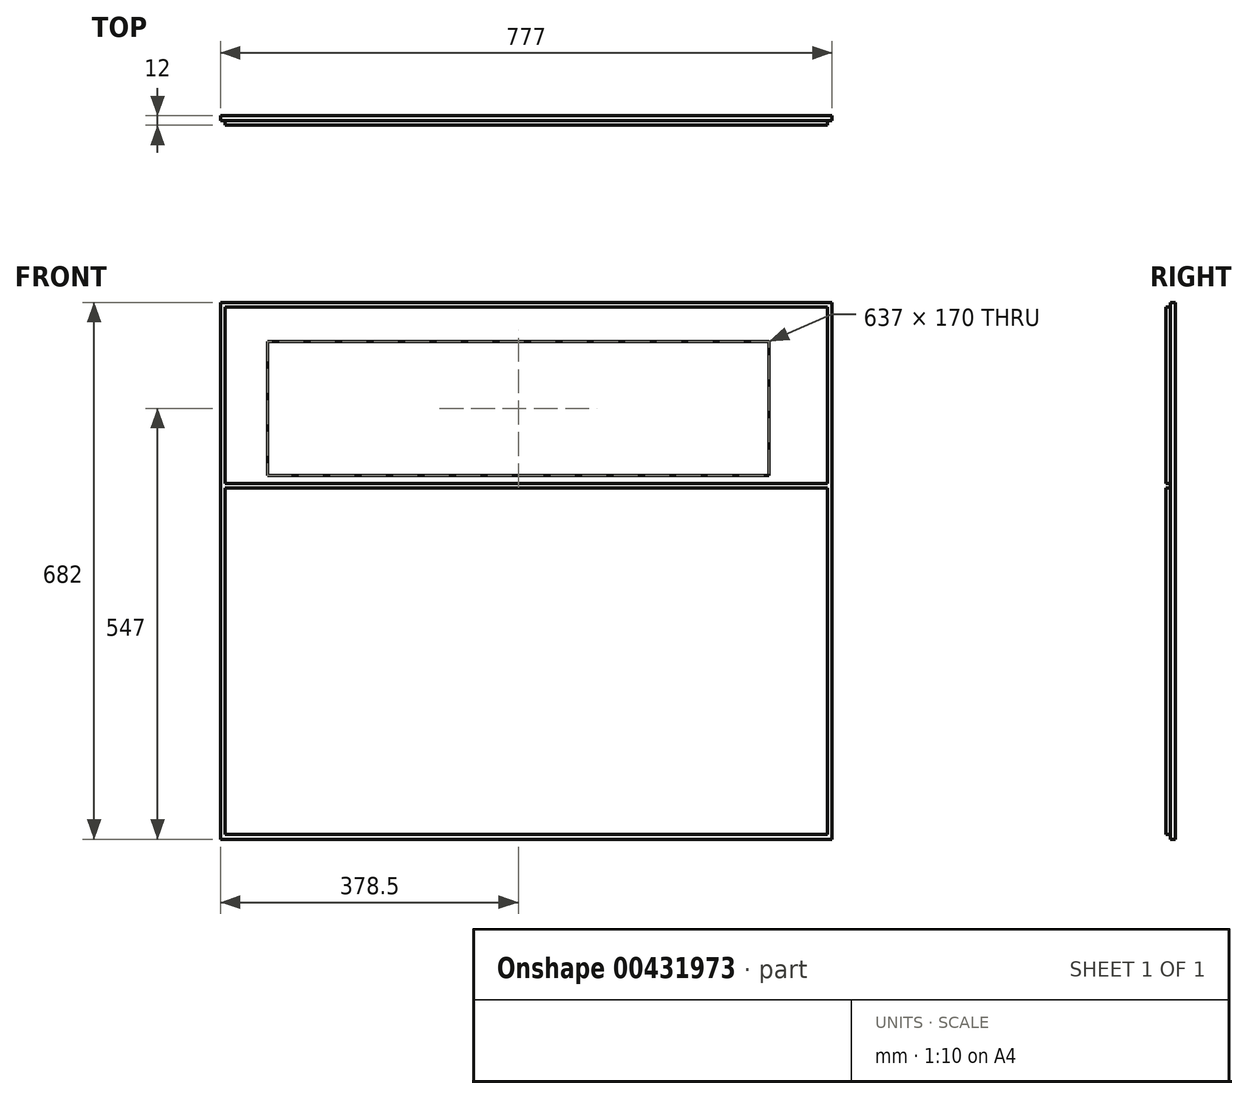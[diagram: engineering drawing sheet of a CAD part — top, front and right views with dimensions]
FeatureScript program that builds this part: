
annotation { "Feature Type Name" : "Feature", "Feature Type Description" : "" }
export const myFeature = defineFeature(function(context is Context, id is Id, definition is map)
    precondition{}
    {
        {
            var Q0;
            Q0=qCreatedBy(makeId("Front.planeOp"),FACE);
            var sketch = newSketch(context, id + "F0", { "sketchPlane" : qUnion([Q0])});
            skPoint(sketch, "E0.middle", {"position": v(0, 0) * mm});
            skLineSegment(sketch, "E1.bottom", {"start": v(388.5, 341) * mm, "end": v(-388.5, 341) * mm});
            skLineSegment(sketch, "E1.top", {"start": v(388.5, -341) * mm, "end": v(-388.5, -341) * mm});
            skLineSegment(sketch, "E1.left", {"start": v(388.5, 341) * mm, "end": v(388.5, -341) * mm});
            skLineSegment(sketch, "E1.right", {"start": v(-388.5, 341) * mm, "end": v(-388.5, -341) * mm});
            skSolve(sketch);
        }
        {
            var Q0;
            Q0=qSketchRegion(id+"F0",true);
            extrude(context, id + "F1", {"entities" : qUnion([Q0]), "depth" : 12 * mm, "offsetDistance" : 25 * mm});
        }
        {
            var Q0;
            Q0=makeQuery(id+"F1.opExtrude","CAP_FACE",FACE,{"disambiguationData":[OSD([sQuery(id+"F0.wireOp",EDGE,"E1.bottom"),sQuery(id+"F0.wireOp",EDGE,"E1.top"),sQuery(id+"F0.wireOp",EDGE,"E1.left"),sQuery(id+"F0.wireOp",EDGE,"E1.right")])],"isStart":false});
            var sketch = newSketch(context, id + "F2", { "sketchPlane" : qUnion([Q0])});
            skLineSegment(sketch, "E2.bottom", {"start": v(-388.5, 111) * mm, "end": v(388.5, 111) * mm});
            skLineSegment(sketch, "E2.top", {"start": v(-388.5, 105) * mm, "end": v(388.5, 105) * mm});
            skLineSegment(sketch, "E2.left", {"start": v(-388.5, 111) * mm, "end": v(-388.5, 105) * mm});
            skLineSegment(sketch, "E2.right", {"start": v(388.5, 111) * mm, "end": v(388.5, 105) * mm});
            skSolve(sketch);
        }
        {
            var Q0;
            Q0=qSketchRegion(id+"F2",true);
            extrude(context, id + "F3", {"entities" : qUnion([Q0]), "operationType" : NewBodyOperationType.REMOVE, "oppositeDirection" : true, "depth" : 6 * mm, "offsetDistance" : 25 * mm});
        }
        {
            var Q0;
            {var subQ0=sQuery(id+"F0.wireOp",EDGE,"E1.bottom");var subQ1=sQuery(id+"F0.wireOp",EDGE,"E1.right");var subQ2=sQuery(id+"F0.wireOp",EDGE,"E1.left");Q0=makeQuery(id+"F3.boolean.opBoolean","SPLIT",FACE,{"disambiguationData":[TD([makeQuery(id+"F1.opExtrude","SWEPT_FACE",FACE,{"disambiguationData":[OSD([subQ0])]})])],"derivedFrom":makeQuery(id+"F1.opExtrude","CAP_FACE",FACE,{"disambiguationData":[OSD([subQ0,sQuery(id+"F0.wireOp",EDGE,"E1.top"),subQ2,subQ1])],"isStart":false})});}
            var sketch = newSketch(context, id + "F4", { "sketchPlane" : qUnion([Q0])});
            skLineSegment(sketch, "E3.bottom", {"start": v(-328.5, 291) * mm, "end": v(308.5, 291) * mm});
            skLineSegment(sketch, "E3.top", {"start": v(-328.5, 121) * mm, "end": v(308.5, 121) * mm});
            skLineSegment(sketch, "E3.left", {"start": v(-328.5, 291) * mm, "end": v(-328.5, 121) * mm});
            skLineSegment(sketch, "E3.right", {"start": v(308.5, 291) * mm, "end": v(308.5, 121) * mm});
            skSolve(sketch);
        }
        {
            var Q0;
            Q0=qSketchRegion(id+"F4",true);
            extrude(context, id + "F5", {"entities" : qUnion([Q0]), "operationType" : NewBodyOperationType.REMOVE, "endBound" : BoundingType.UP_TO_NEXT, "oppositeDirection" : true, "depth" : 25 * mm});
        }
        {
            var Q0;
            {var subQ0=sQuery(id+"F0.wireOp",EDGE,"E1.bottom");var subQ1=sQuery(id+"F0.wireOp",EDGE,"E1.right");var subQ2=sQuery(id+"F0.wireOp",EDGE,"E1.left");Q0=makeQuery(id+"F3.boolean.opBoolean","SPLIT",FACE,{"disambiguationData":[TD([makeQuery(id+"F1.opExtrude","SWEPT_FACE",FACE,{"disambiguationData":[OSD([subQ0])]})])],"derivedFrom":makeQuery(id+"F1.opExtrude","CAP_FACE",FACE,{"disambiguationData":[OSD([subQ0,sQuery(id+"F0.wireOp",EDGE,"E1.top"),subQ2,subQ1])],"isStart":false})});}
            var sketch = newSketch(context, id + "F6", { "sketchPlane" : qUnion([Q0])});
            skLineSegment(sketch, "E4.bottom", {"start": v(-388.5, 341) * mm, "end": v(388.5, 341) * mm});
            skLineSegment(sketch, "E4.top", {"start": v(-388.5, 335) * mm, "end": v(388.5, 335) * mm});
            skLineSegment(sketch, "E4.left", {"start": v(-388.5, 341) * mm, "end": v(-388.5, 335) * mm});
            skLineSegment(sketch, "E4.right", {"start": v(388.5, 341) * mm, "end": v(388.5, 335) * mm});
            skSolve(sketch);
        }
        {
            var Q0;
            Q0=makeQuery(id+"F6.imprint","IMPRINT",FACE,{"disambiguationData":[TD([[makeQuery(id+"F6.imprint","IMPRINT",EDGE,{"derivedFrom":sQuery(id+"F6.wireOp",EDGE,"E4.bottom")}),1.0]])]});
            extrude(context, id + "F7", {"entities" : qUnion([Q0]), "operationType" : NewBodyOperationType.REMOVE, "oppositeDirection" : true, "depth" : 6 * mm, "offsetDistance" : 25 * mm});
        }
        {
            var Q0;
            {var subQ0=sQuery(id+"F0.wireOp",EDGE,"E1.top");var subQ1=sQuery(id+"F0.wireOp",EDGE,"E1.left");var subQ2=sQuery(id+"F0.wireOp",EDGE,"E1.right");Q0=makeQuery(id+"F3.boolean.opBoolean","SPLIT",FACE,{"disambiguationData":[TD([makeQuery(id+"F1.opExtrude","SWEPT_FACE",FACE,{"disambiguationData":[OSD([subQ0])]})])],"derivedFrom":makeQuery(id+"F1.opExtrude","CAP_FACE",FACE,{"disambiguationData":[OSD([sQuery(id+"F0.wireOp",EDGE,"E1.bottom"),subQ0,subQ1,subQ2])],"isStart":false})});}
            var sketch = newSketch(context, id + "F8", { "sketchPlane" : qUnion([Q0])});
            skLineSegment(sketch, "E5.bottom", {"start": v(-388.5, -341) * mm, "end": v(-382.5, -341) * mm});
            skLineSegment(sketch, "E5.top", {"start": v(-388.5, 335) * mm, "end": v(-382.5, 335) * mm});
            skLineSegment(sketch, "E5.left", {"start": v(-388.5, -341) * mm, "end": v(-388.5, 335) * mm});
            skLineSegment(sketch, "E5.right", {"start": v(-382.5, -341) * mm, "end": v(-382.5, 335) * mm});
            skSolve(sketch);
        }
        {
            var Q0;
            Q0 = qSketchRegion(id + "F8", true);
            extrude(context, id + "F9", {"entities" : qUnion([Q0]), "operationType" : NewBodyOperationType.REMOVE, "oppositeDirection" : true, "depth" : 6 * mm, "offsetDistance" : 25 * mm});
        }
        {
            var Q0;
            {var subQ0=sQuery(id+"F0.wireOp",EDGE,"E1.top");var subQ1=sQuery(id+"F0.wireOp",EDGE,"E1.left");var subQ2=sQuery(id+"F0.wireOp",EDGE,"E1.right");Q0=makeQuery(id+"F3.boolean.opBoolean","SPLIT",FACE,{"disambiguationData":[TD([makeQuery(id+"F1.opExtrude","SWEPT_FACE",FACE,{"disambiguationData":[OSD([subQ0])]})])],"derivedFrom":makeQuery(id+"F1.opExtrude","CAP_FACE",FACE,{"disambiguationData":[OSD([sQuery(id+"F0.wireOp",EDGE,"E1.bottom"),subQ0,subQ1,subQ2])],"isStart":false})});}
            var sketch = newSketch(context, id + "F10", { "sketchPlane" : qUnion([Q0])});
            skLineSegment(sketch, "E6.bottom", {"start": v(388.5, -341) * mm, "end": v(382.5, -341) * mm});
            skLineSegment(sketch, "E6.top", {"start": v(388.5, 335) * mm, "end": v(382.5, 335) * mm});
            skLineSegment(sketch, "E6.left", {"start": v(388.5, -341) * mm, "end": v(388.5, 335) * mm});
            skLineSegment(sketch, "E6.right", {"start": v(382.5, -341) * mm, "end": v(382.5, 335) * mm});
            skSolve(sketch);
        }
        {
            var Q0;
            Q0 = qSketchRegion(id + "F10", true);
            extrude(context, id + "F11", {"entities" : qUnion([Q0]), "operationType" : NewBodyOperationType.REMOVE, "oppositeDirection" : true, "depth" : 6 * mm, "offsetDistance" : 25 * mm});
        }
        {
            var Q0;
            {var subQ0=sQuery(id+"F0.wireOp",EDGE,"E1.top");var subQ1=sQuery(id+"F0.wireOp",EDGE,"E1.left");var subQ2=sQuery(id+"F0.wireOp",EDGE,"E1.right");Q0=makeQuery(id+"F3.boolean.opBoolean","SPLIT",FACE,{"disambiguationData":[TD([makeQuery(id+"F1.opExtrude","SWEPT_FACE",FACE,{"disambiguationData":[OSD([subQ0])]})])],"derivedFrom":makeQuery(id+"F1.opExtrude","CAP_FACE",FACE,{"disambiguationData":[OSD([sQuery(id+"F0.wireOp",EDGE,"E1.bottom"),subQ0,subQ1,subQ2])],"isStart":false})});}
            var sketch = newSketch(context, id + "F12", { "sketchPlane" : qUnion([Q0])});
            skLineSegment(sketch, "E7.bottom", {"start": v(-382.5, -341) * mm, "end": v(382.5, -341) * mm});
            skLineSegment(sketch, "E7.top", {"start": v(-382.5, -335) * mm, "end": v(382.5, -335) * mm});
            skLineSegment(sketch, "E7.left", {"start": v(-382.5, -341) * mm, "end": v(-382.5, -335) * mm});
            skLineSegment(sketch, "E7.right", {"start": v(382.5, -341) * mm, "end": v(382.5, -335) * mm});
            skSolve(sketch);
        }
        {
            var Q0;
            Q0 = qSketchRegion(id + "F12", true);
            extrude(context, id + "F13", {"entities" : qUnion([Q0]), "operationType" : NewBodyOperationType.REMOVE, "oppositeDirection" : true, "depth" : 6 * mm, "offsetDistance" : 25 * mm});
        }
    });
